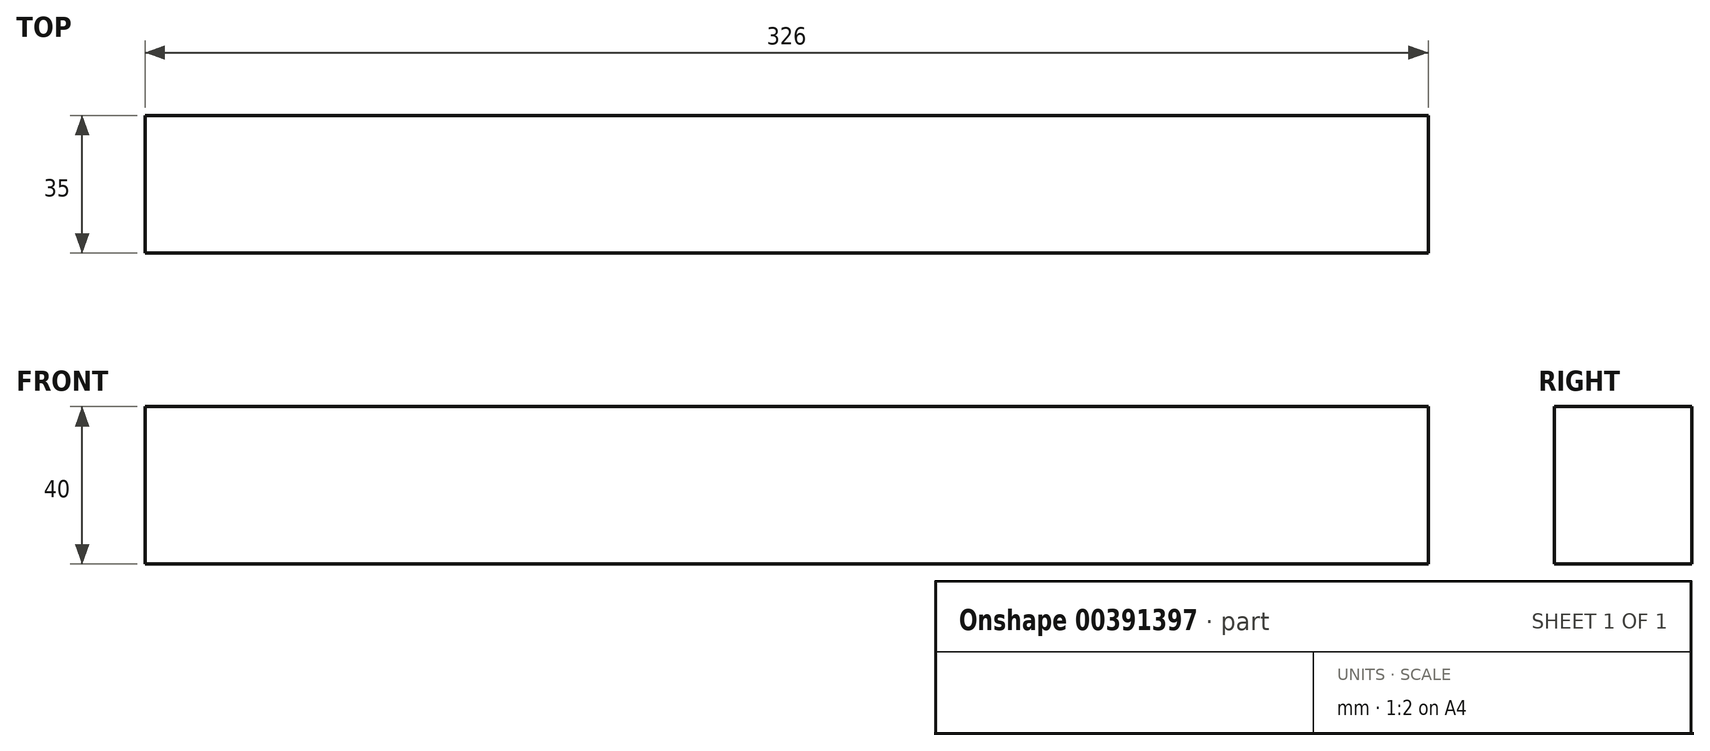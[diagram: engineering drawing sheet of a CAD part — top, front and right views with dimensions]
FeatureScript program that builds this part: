
annotation { "Feature Type Name" : "Feature", "Feature Type Description" : "" }
export const myFeature = defineFeature(function(context is Context, id is Id, definition is map)
    precondition{}
    {
        {
            var Q0;
            Q0=qCreatedBy(makeId("Right.planeOp"),FACE);
            var sketch = newSketch(context, id + "F0", { "sketchPlane" : qUnion([Q0])});
            skLineSegment(sketch, "E0.bottom", {"start": v(35, 47.25) * mm, "end": v(0, 47.25) * mm});
            skLineSegment(sketch, "E0.top", {"start": v(35, 7.25) * mm, "end": v(0, 7.25) * mm});
            skLineSegment(sketch, "E0.left", {"start": v(35, 47.25) * mm, "end": v(35, 7.25) * mm});
            skLineSegment(sketch, "E0.right", {"start": v(0, 47.25) * mm, "end": v(0, 7.25) * mm});
            skSolve(sketch);
        }
        {
            var Q0;
            Q0=qSketchRegion(id+"F0",true);
            extrude(context, id + "F1", {"entities" : qUnion([Q0]), "depth" : 326 * mm});
        }
    });
